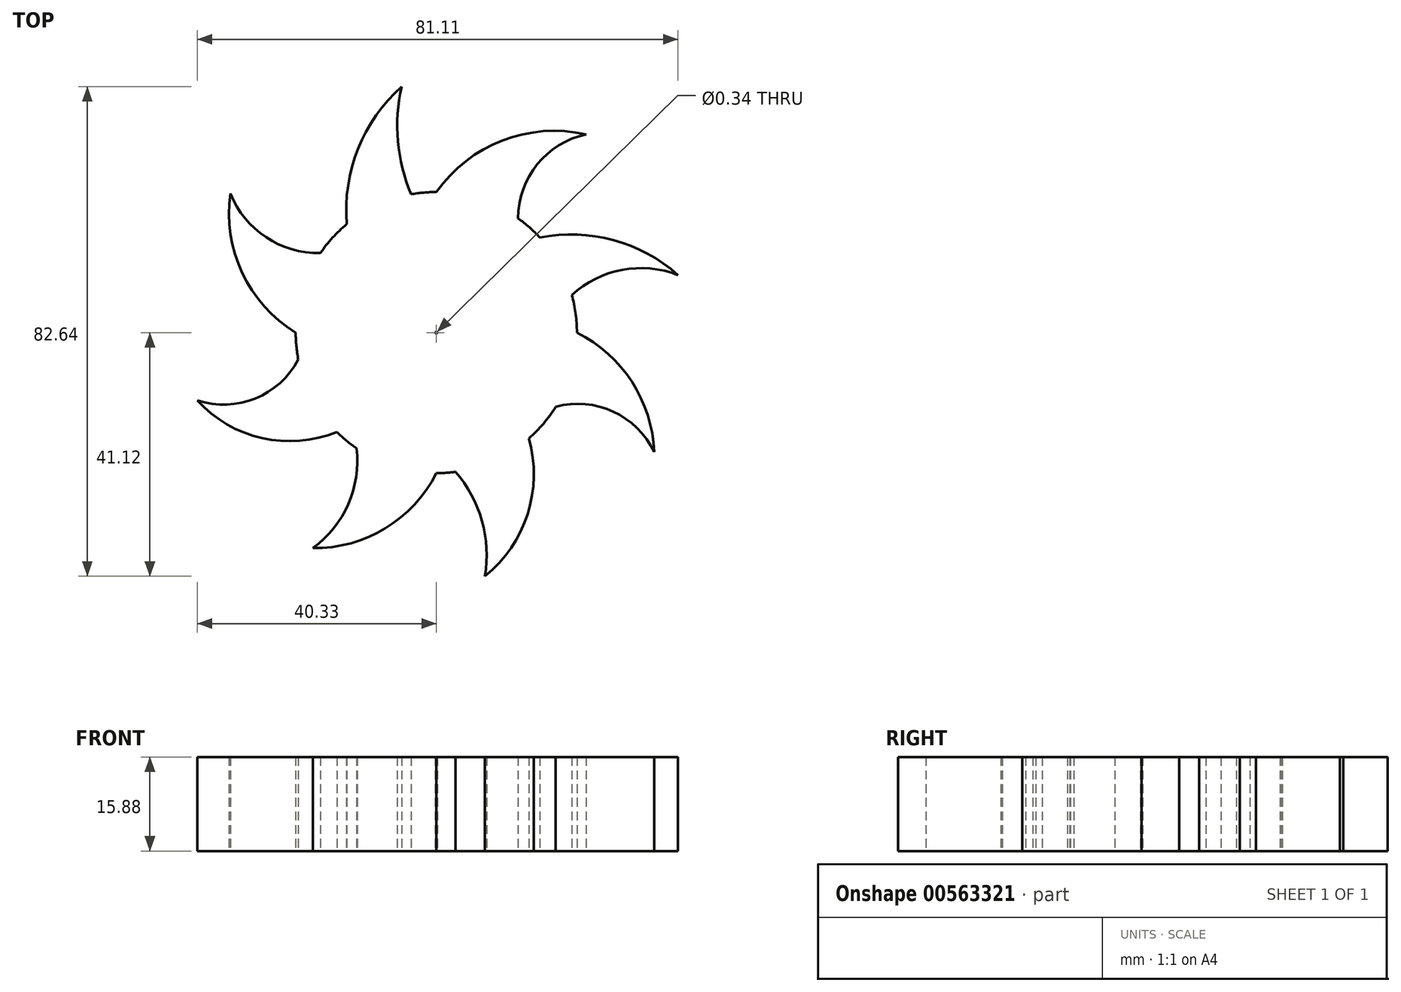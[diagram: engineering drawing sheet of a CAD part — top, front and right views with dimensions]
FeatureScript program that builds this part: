
annotation { "Feature Type Name" : "Feature", "Feature Type Description" : "" }
export const myFeature = defineFeature(function(context is Context, id is Id, definition is map)
    precondition{}
    {
        {
            var Q0;
            Q0=qCreatedBy(makeId("Top.planeOp"),FACE);
            var sketch = newSketch(context, id + "F0", { "sketchPlane" : qUnion([Q0])});
            skCircle(sketch, "E0", {"center": v(0, 0) * mm, "radius": 23.72 * mm});
            skArc(sketch, "E1", {"start": v(25.27, 33.45) * mm, "mid": v(11.16, 32.43) * mm, "end": v(0, 23.72) * mm});
            skArc(sketch, "E2", {"start": v(25.27, 33.45) * mm, "mid": v(17.03, 28.4) * mm, "end": v(13.8, 19.3) * mm});
            skArc(sketch, "E3", {"start": v(36.77, -20.15) * mm, "mid": v(33, -8.3) * mm, "end": v(23.72, 0) * mm});
            skArc(sketch, "E4", {"start": v(36.77, -20.15) * mm, "mid": v(29.84, -13.34) * mm, "end": v(20.15, -12.52) * mm});
            skArc(sketch, "E5", {"start": v(-20.85, -36.37) * mm, "mid": v(-8.6, -33.05) * mm, "end": v(0, -23.72) * mm});
            skArc(sketch, "E6", {"start": v(-20.85, -36.37) * mm, "mid": v(-14.86, -28.96) * mm, "end": v(-13.46, -19.54) * mm});
            skArc(sketch, "E7", {"start": v(-34.73, 23.49) * mm, "mid": v(-32.76, 10.09) * mm, "end": v(-23.72, 0) * mm});
            skArc(sketch, "E8", {"start": v(-34.73, 23.49) * mm, "mid": v(-28.72, 16.08) * mm, "end": v(-19.56, 13.42) * mm});
            skArc(sketch, "E9", {"start": v(-5.84, 41.52) * mm, "mid": v(-13.21, 31) * mm, "end": v(-15.1, 18.3) * mm});
            skArc(sketch, "E10", {"start": v(-5.84, 41.52) * mm, "mid": v(-6.48, 32.3) * mm, "end": v(-4.26, 23.34) * mm});
            skArc(sketch, "E11", {"start": v(40.78, 9.72) * mm, "mid": v(29.88, 15.62) * mm, "end": v(17.49, 16.03) * mm});
            skArc(sketch, "E12", {"start": v(40.78, 9.72) * mm, "mid": v(31.34, 10.58) * mm, "end": v(22.86, 6.33) * mm});
            skArc(sketch, "E13", {"start": v(8.2, -41.12) * mm, "mid": v(15.4, -30.61) * mm, "end": v(15.6, -17.87) * mm});
            skArc(sketch, "E14", {"start": v(8.2, -41.12) * mm, "mid": v(7.69, -31.76) * mm, "end": v(3.24, -23.5) * mm});
            skArc(sketch, "E15", {"start": v(-40.33, -11.45) * mm, "mid": v(-29.4, -17.8) * mm, "end": v(-16.79, -16.76) * mm});
            skArc(sketch, "E16", {"start": v(-40.33, -11.45) * mm, "mid": v(-30.54, -11.11) * mm, "end": v(-23.29, -4.53) * mm});
            skSolve(sketch);
        }
        {
            var Q0;
            {var subQ0=sQuery(id+"F0.wireOp",EDGE,"E0");var subQ8=makeQuery(id+"F0.imprint","INTERSECT",VERTEX,{"derivedFrom":[subQ0,sQuery(id+"F0.wireOp",EDGE,"E3")]});Q0=makeQuery(id+"F0.imprint","IMPRINT",FACE,{"disambiguationData":[TD([[makeQuery(id+"F0.imprint","IMPRINT",EDGE,{"disambiguationData":[TD([[subQ8,-1.0]])],"derivedFrom":subQ0}),1.0]])]});}
            extrude(context, id + "F1", {"entities" : qUnion([Q0]), "depth" : 6.35 * mm, "offsetDistance" : 25.4 * mm});
        }
        {
            var Q0;
            {var subQ0=sQuery(id+"F0.wireOp",EDGE,"E7");Q0=makeQuery(id+"F0.imprint","IMPRINT",FACE,{"disambiguationData":[TD([[makeQuery(id+"F0.imprint","IMPRINT",EDGE,{"derivedFrom":subQ0}),1.0]])]});}
            var Q1;
            {var subQ0=sQuery(id+"F0.wireOp",EDGE,"E15");Q1=makeQuery(id+"F0.imprint","IMPRINT",FACE,{"disambiguationData":[TD([[makeQuery(id+"F0.imprint","IMPRINT",EDGE,{"derivedFrom":subQ0}),1.0]])]});}
            var Q2;
            {var subQ0=sQuery(id+"F0.wireOp",EDGE,"E5");Q2=makeQuery(id+"F0.imprint","IMPRINT",FACE,{"disambiguationData":[TD([[makeQuery(id+"F0.imprint","IMPRINT",EDGE,{"derivedFrom":subQ0}),1.0]])]});}
            var Q3;
            {var subQ0=sQuery(id+"F0.wireOp",EDGE,"E13");Q3=makeQuery(id+"F0.imprint","IMPRINT",FACE,{"disambiguationData":[TD([[makeQuery(id+"F0.imprint","IMPRINT",EDGE,{"derivedFrom":subQ0}),1.0]])]});}
            var Q4;
            {var subQ0=sQuery(id+"F0.wireOp",EDGE,"E3");Q4=makeQuery(id+"F0.imprint","IMPRINT",FACE,{"disambiguationData":[TD([[makeQuery(id+"F0.imprint","IMPRINT",EDGE,{"derivedFrom":subQ0}),1.0]])]});}
            var Q5;
            {var subQ0=sQuery(id+"F0.wireOp",EDGE,"E11");Q5=makeQuery(id+"F0.imprint","IMPRINT",FACE,{"disambiguationData":[TD([[makeQuery(id+"F0.imprint","IMPRINT",EDGE,{"derivedFrom":subQ0}),1.0]])]});}
            var Q6;
            {var subQ0=sQuery(id+"F0.wireOp",EDGE,"E1");Q6=makeQuery(id+"F0.imprint","IMPRINT",FACE,{"disambiguationData":[TD([[makeQuery(id+"F0.imprint","IMPRINT",EDGE,{"derivedFrom":subQ0}),1.0]])]});}
            var Q7;
            {var subQ0=sQuery(id+"F0.wireOp",EDGE,"E9");Q7=makeQuery(id+"F0.imprint","IMPRINT",FACE,{"disambiguationData":[TD([[makeQuery(id+"F0.imprint","IMPRINT",EDGE,{"derivedFrom":subQ0}),1.0]])]});}
            var Q8;
            {var subQ0=sQuery(id+"F0.wireOp",EDGE,"E0");var subQ8=makeQuery(id+"F0.imprint","INTERSECT",VERTEX,{"derivedFrom":[subQ0,sQuery(id+"F0.wireOp",EDGE,"E3")]});Q8=makeQuery(id+"F0.imprint","IMPRINT",FACE,{"disambiguationData":[TD([[makeQuery(id+"F0.imprint","IMPRINT",EDGE,{"disambiguationData":[TD([[subQ8,-1.0]])],"derivedFrom":subQ0}),1.0]])]});}
            extrude(context, id + "F2", {"entities" : qUnion([Q0, Q1, Q2, Q3, Q4, Q5, Q6, Q7, Q8]), "operationType" : NewBodyOperationType.ADD, "depth" : 15.88 * mm, "offsetDistance" : 25.4 * mm});
        }
        {
            var Q0;
            Q0=qCreatedBy(makeId("Top.planeOp"),FACE);
            var sketch = newSketch(context, id + "F3", { "sketchPlane" : qUnion([Q0])});
            skPoint(sketch, "E17", {"position": v(0, 0) * mm});
            skCircle(sketch, "E18", {"center": v(0, 0) * mm, "radius": 0.4 * mm});
            skSolve(sketch);
        }
        {
            var Q0;
            Q0=sQuery(id+"F3.wireOp",VERTEX,"E17");
            var Q1;
            Q1=makeQuery(id+"F1.opExtrude","SWEPT_BODY",BODY,{"disambiguationData":[OSD([sQuery(id+"F0.wireOp",EDGE,"E0")])]});
            hole(context, id + "F4", {"style" : HoleStyle.SIMPLE, "endStyle" : HoleEndStyle.THROUGH, "oppositeDirection" : true, "holeDiameter" : 0.34 * mm, "isTappedThrough" : true, "tappedDepth" : 12.7 * mm, "tapClearance" : 3, "locations" : qUnion([Q0]), "scope" : qUnion([Q1])});
        }
    });
